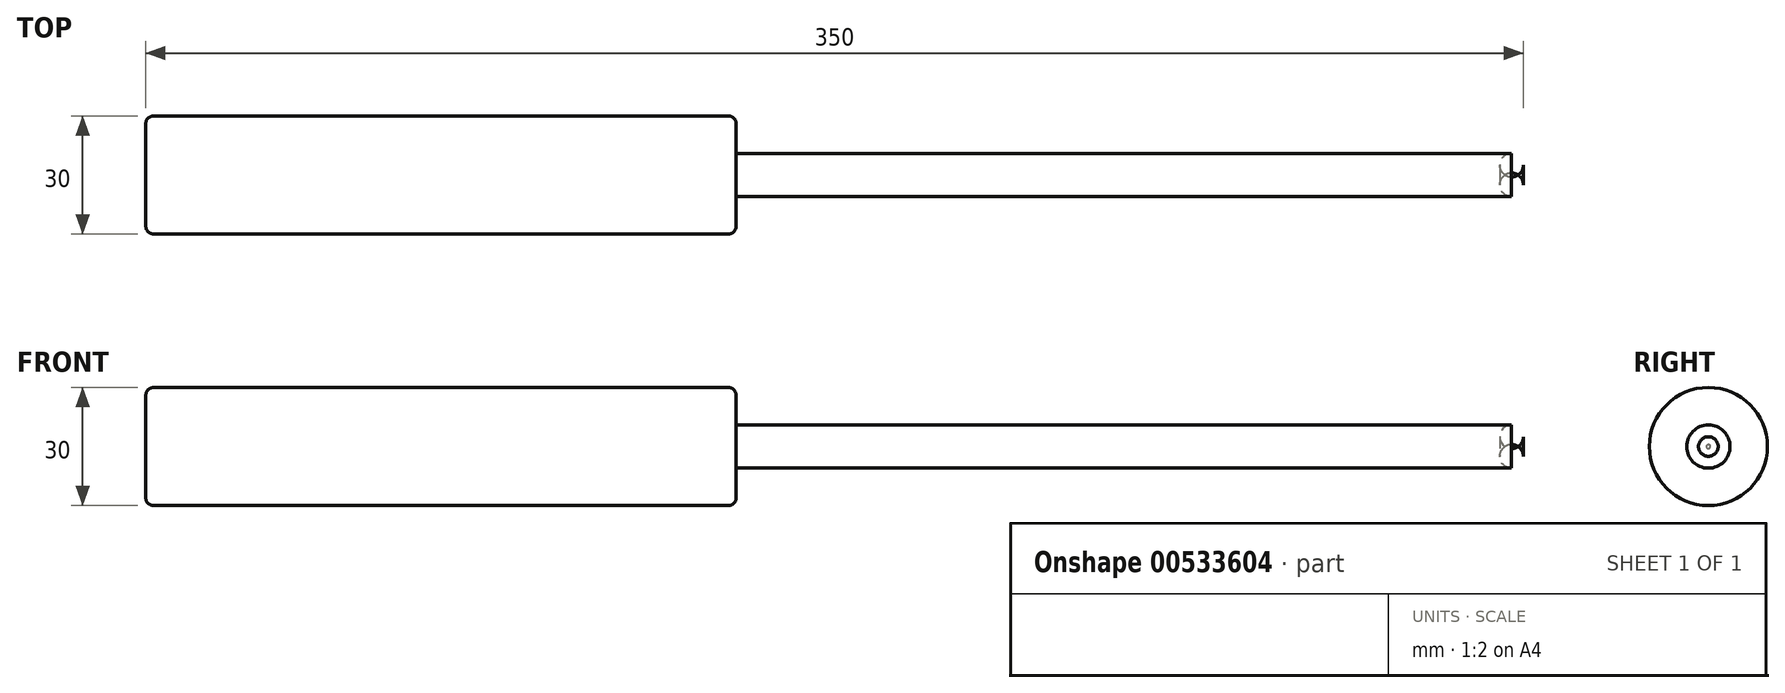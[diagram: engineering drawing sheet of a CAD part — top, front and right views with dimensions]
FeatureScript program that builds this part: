
annotation { "Feature Type Name" : "Feature", "Feature Type Description" : "" }
export const myFeature = defineFeature(function(context is Context, id is Id, definition is map)
    precondition{}
    {
        {
            var Q0;
            Q0=qCreatedBy(makeId("Front.planeOp"),FACE);
            var sketch = newSketch(context, id + "F0", { "sketchPlane" : qUnion([Q0])});
            skLineSegment(sketch, "E0", {"start": v(-50.2, 0) * mm, "end": v(-50.2, 15) * mm});
            skLineSegment(sketch, "E1", {"start": v(-50.2, 15) * mm, "end": v(99.8, 15) * mm});
            skLineSegment(sketch, "E2", {"start": v(99.8, 15) * mm, "end": v(99.8, 5.5) * mm});
            skLineSegment(sketch, "E3", {"start": v(99.8, 5.5) * mm, "end": v(299.8, 5.5) * mm});
            skLineSegment(sketch, "E4", {"start": v(299.8, 5.5) * mm, "end": v(299.8, 0) * mm});
            skLineSegment(sketch, "E5", {"start": v(299.8, 0) * mm, "end": v(-50.2, 0) * mm});
            skSolve(sketch);
        }
        {
            var Q0;
            Q0=makeQuery(id+"F0.imprint","IMPRINT",FACE,{"disambiguationData":[TD([[makeQuery(id+"F0.imprint","IMPRINT",EDGE,{"derivedFrom":sQuery(id+"F0.wireOp",EDGE,"E0")}),-1.0]])]});
            var Q1;
            Q1=sQuery(id+"F0.wireOp",EDGE,"E5");
            revolve(context, id + "F1", {"entities" : qUnion([Q0]), "axis" : qUnion([Q1]), "revolveType" : RevolveType.FULL});
        }
        {
            var Q0;
            Q0=makeQuery(id+"F1.opRevolve","SWEPT_EDGE",EDGE,{"disambiguationData":[OSD([sQuery(id+"F0.wireOp",EDGE,"E3"),sQuery(id+"F0.wireOp",EDGE,"E4")])]});
            fillet(context, id + "F2", {"entities" : qUnion([Q0]), "radius" : 3 * mm, "tangentPropagation" : true, "allowEdgeOverflow" : false});
        }
        {
            var Q0;
            Q0=makeQuery(id+"F1.opRevolve","SWEPT_EDGE",EDGE,{"disambiguationData":[OSD([sQuery(id+"F0.wireOp",EDGE,"E1"),sQuery(id+"F0.wireOp",EDGE,"E2")])]});
            var Q1;
            Q1=makeQuery(id+"F1.opRevolve","SWEPT_EDGE",EDGE,{"disambiguationData":[OSD([sQuery(id+"F0.wireOp",EDGE,"E0"),sQuery(id+"F0.wireOp",EDGE,"E1")])]});
            fillet(context, id + "F3", {"entities" : qUnion([Q0, Q1]), "radius" : 2 * mm, "tangentPropagation" : true, "allowEdgeOverflow" : false});
        }
    });
